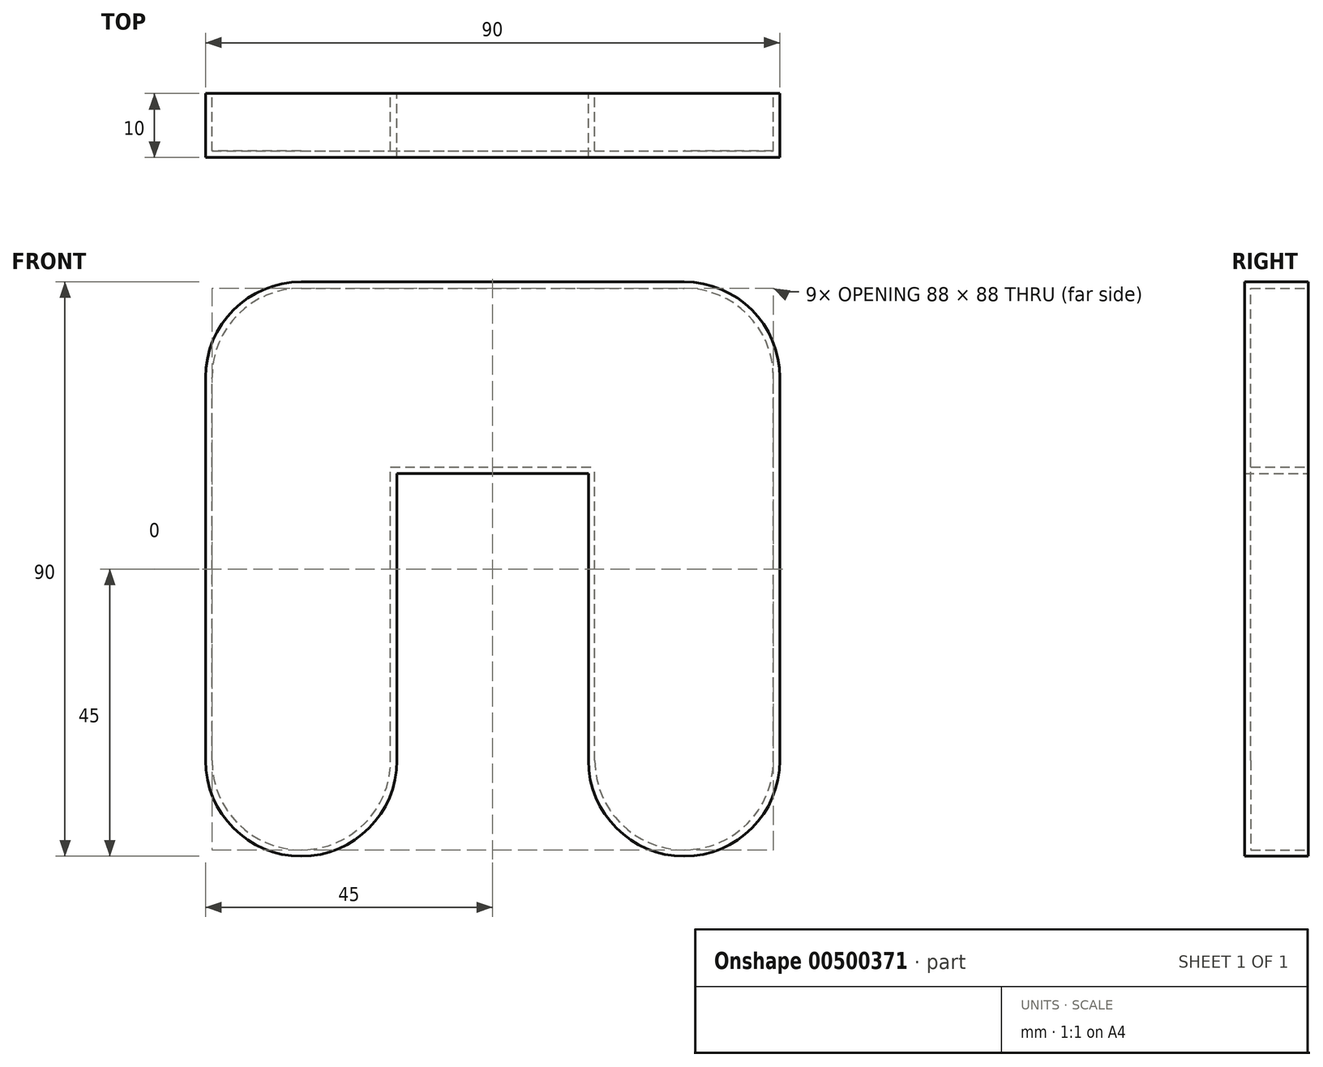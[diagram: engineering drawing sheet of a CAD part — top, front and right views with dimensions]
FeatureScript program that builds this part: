
annotation { "Feature Type Name" : "Feature", "Feature Type Description" : "" }
export const myFeature = defineFeature(function(context is Context, id is Id, definition is map)
    precondition{}
    {
        {
            var Q0;
            Q0=qCreatedBy(makeId("Front.planeOp"),FACE);
            var sketch = newSketch(context, id + "F0", { "sketchPlane" : qUnion([Q0])});
            skLineSegment(sketch, "E0.bottom", {"start": v(15, 0) * mm, "end": v(15, 0) * mm});
            skLineSegment(sketch, "E0.top", {"start": v(15, 90) * mm, "end": v(75, 90) * mm});
            skLineSegment(sketch, "E0.left", {"start": v(0, 15) * mm, "end": v(0, 75) * mm});
            skLineSegment(sketch, "E0.right", {"start": v(90, 15) * mm, "end": v(90, 75) * mm});
            skLineSegment(sketch, "E1", {"start": v(30, 15) * mm, "end": v(30, 60) * mm});
            skLineSegment(sketch, "E2", {"start": v(60, 15) * mm, "end": v(60, 60) * mm});
            skLineSegment(sketch, "E3", {"start": v(30, 60) * mm, "end": v(60, 60) * mm});
            skLineSegment(sketch, "E4.trimOffspring", {"start": v(75, 0) * mm, "end": v(75, 0) * mm});
            skPoint(sketch, "E5.visualSharp", {"position": v(0, 90) * mm});
            skArc(sketch, "E5.filletArc", {"start": v(15, 90) * mm, "mid": v(4.4, 85.6) * mm, "end": v(0, 75) * mm});
            skPoint(sketch, "E6.visualSharp", {"position": v(90, 90) * mm});
            skArc(sketch, "E6.filletArc", {"start": v(90, 75) * mm, "mid": v(85.6, 85.6) * mm, "end": v(75, 90) * mm});
            skPoint(sketch, "E7.visualSharp", {"position": v(60, 0) * mm});
            skArc(sketch, "E7.filletArc", {"start": v(60, 15) * mm, "mid": v(64.4, 4.4) * mm, "end": v(75, 0) * mm});
            skPoint(sketch, "E8.visualSharp", {"position": v(90, 0) * mm});
            skArc(sketch, "E8.filletArc", {"start": v(75, 0) * mm, "mid": v(85.6, 4.4) * mm, "end": v(90, 15) * mm});
            skPoint(sketch, "E9.visualSharp", {"position": v(0, 0) * mm});
            skArc(sketch, "E9.filletArc", {"start": v(0, 15) * mm, "mid": v(4.4, 4.4) * mm, "end": v(15, 0) * mm});
            skPoint(sketch, "E10.visualSharp", {"position": v(30, 0) * mm});
            skArc(sketch, "E10.filletArc", {"start": v(15, 0) * mm, "mid": v(25.6, 4.4) * mm, "end": v(30, 15) * mm});
            skSolve(sketch);
        }
        {
            var Q0;
            Q0=makeQuery(id+"F0.imprint","IMPRINT",FACE,{"disambiguationData":[TD([[makeQuery(id+"F0.imprint","IMPRINT",EDGE,{"derivedFrom":sQuery(id+"F0.wireOp",EDGE,"E0.top")}),-1.0]])]});
            extrude(context, id + "F1", {"entities" : qUnion([Q0]), "depth" : 10 * mm});
        }
        {
            var Q0;
            Q0=makeQuery(id+"F1.opExtrude","CAP_FACE",FACE,{"disambiguationData":[OSD([sQuery(id+"F0.wireOp",EDGE,"E0.top"),sQuery(id+"F0.wireOp",EDGE,"E0.left"),sQuery(id+"F0.wireOp",EDGE,"E0.right"),sQuery(id+"F0.wireOp",EDGE,"E1"),sQuery(id+"F0.wireOp",EDGE,"E2"),sQuery(id+"F0.wireOp",EDGE,"E3"),sQuery(id+"F0.wireOp",EDGE,"E5.filletArc"),sQuery(id+"F0.wireOp",EDGE,"E6.filletArc"),sQuery(id+"F0.wireOp",EDGE,"E7.filletArc"),sQuery(id+"F0.wireOp",EDGE,"E8.filletArc"),sQuery(id+"F0.wireOp",EDGE,"E9.filletArc"),sQuery(id+"F0.wireOp",EDGE,"E10.filletArc")])],"isStart":true});
            shell(context, id + "F2", {"entities" : qUnion([Q0]), "thickness" : 1 * mm});
        }
    });
